# Revit family: 7021986300154_Luna Deco 3 U - generic
name_source: partatom
category: Lighting Fixtures
units: mm (PartAtom-declared; Revit-internal decimal feet)

## family parameters
Always vertical = Yes
Cut with Voids When Loaded = No
Light Source = No
OmniClass Number = 23.80.70.00
OmniClass Title = Lighting
Part Type = Normal
Room Calculation Point = No
Round Connector Dimension = Use Diameter
Shared = No
Work Plane-Based = No

## types (1)
- Luna Deco 3 0
    Area = 0,01 m²
    Center of Gravity = X: 0,000 mm Y: -9,212 mm Z: 0,001 mm
    Default Elevation = 0 mm  [stored 0 ft]
    Density = 1000,00 kg/m³
    Description = Luna Deco 3 U
    Design Status = 1
    Designer = she
    Manufacturer = Sg Armaturen
    Mass = 0,06 kg
    Material = Generic
    Model = Luna Deco 3 U
    Part Number = Luna Deco 3 U
    Preprocessor = SwSTEP 2.0
    Requested Accuracy = Low
    Revision Number = ANY
    Sending System = SolidWorks 2017
    Title = Luna Deco 3 O.STEP
    URL = https://www.sg-as.com
    Volume = 0,00 m³

note: [stored X ft] marks values corroborated as IEEE doubles in the binary element streams (Revit-internal decimal feet)

## geometry (parser evidence)
native form markers: Sweep x3
no freeform markers — native parametric forms only
